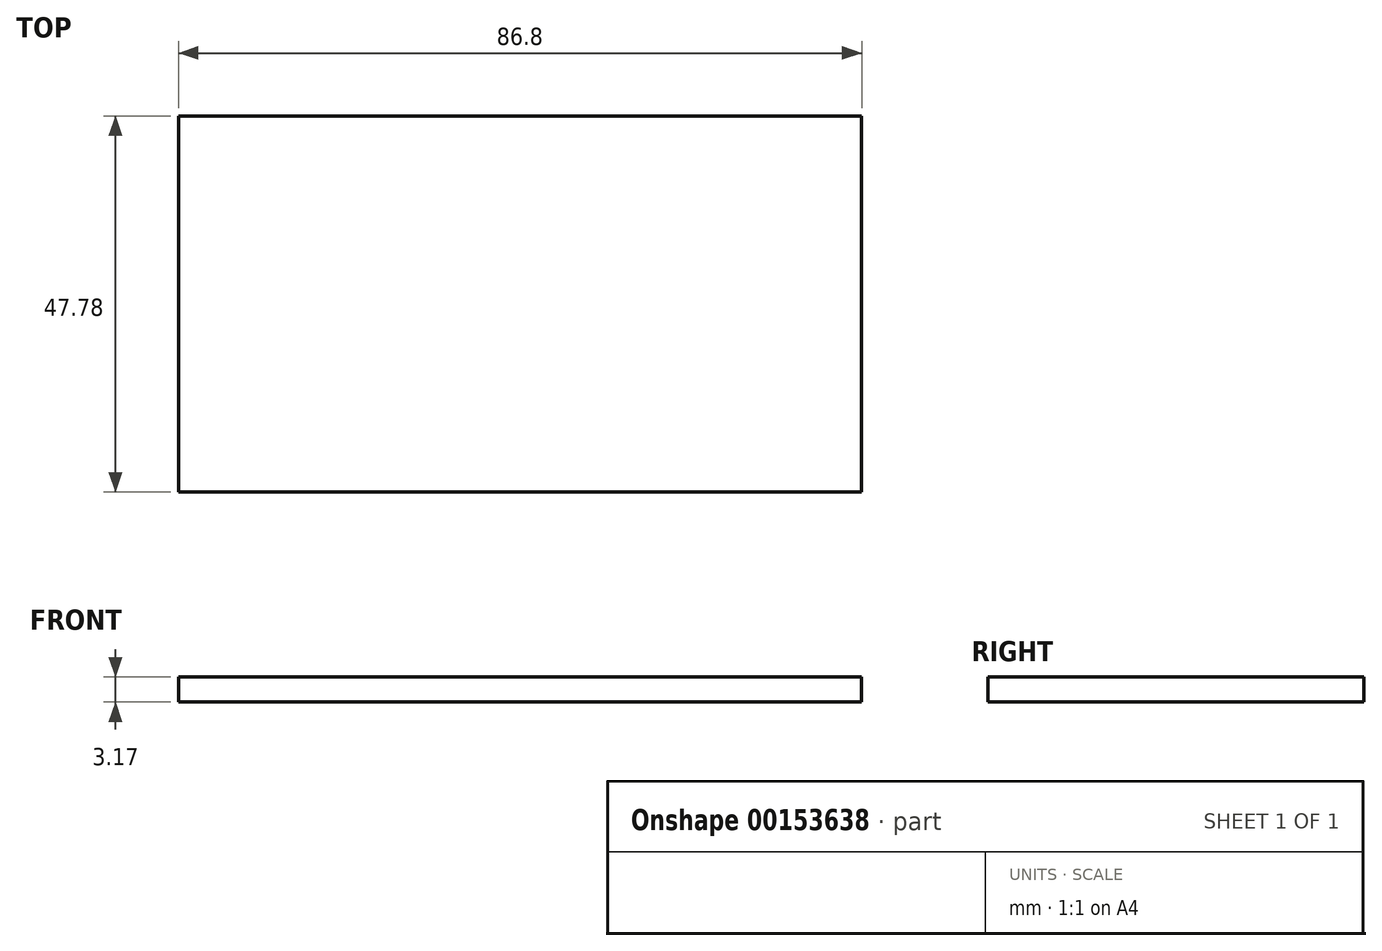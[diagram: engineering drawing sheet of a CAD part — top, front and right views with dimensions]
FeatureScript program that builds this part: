
annotation { "Feature Type Name" : "Feature", "Feature Type Description" : "" }
export const myFeature = defineFeature(function(context is Context, id is Id, definition is map)
    precondition{}
    {
        {
            var Q0;
            Q0=qCreatedBy(makeId("Top.planeOp"),FACE);
            var sketch = newSketch(context, id + "F0", { "sketchPlane" : qUnion([Q0])});
            skLineSegment(sketch, "E0.bottom", {"start": v(-35.2, 23.18) * mm, "end": v(51.6, 23.18) * mm});
            skLineSegment(sketch, "E0.top", {"start": v(-35.2, -24.6) * mm, "end": v(51.6, -24.6) * mm});
            skLineSegment(sketch, "E0.left", {"start": v(-35.2, 23.18) * mm, "end": v(-35.2, -24.6) * mm});
            skLineSegment(sketch, "E0.right", {"start": v(51.6, 23.18) * mm, "end": v(51.6, -24.6) * mm});
            skSolve(sketch);
        }
        {
            var Q0;
            Q0 = qSketchRegion(id + "F0", true);
            extrude(context, id + "F1", {"entities" : qUnion([Q0]), "depth" : 3.17 * mm});
        }
    });
